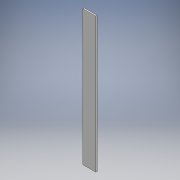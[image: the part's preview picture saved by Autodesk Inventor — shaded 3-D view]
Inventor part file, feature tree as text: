
AUTODESK INVENTOR PART (.ipt)
format: ipt  version: 2018 (Build 220112000, 112)  size: 93,184 bytes
history: native  units: mm
features: other x1, extrude x1, sketch x1
ambient origin geometry x8: Origin, YZ Plane, XZ Plane, XY Plane, X Axis, Y Axis, Z Axis, Center Point
bodies: Body1 (feature_tree)
feature tree (3):
  other  "ソリッド1"
  extrude  "押し出し1"  Depth=302.0mm
  sketch  "スケッチ1"
